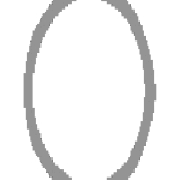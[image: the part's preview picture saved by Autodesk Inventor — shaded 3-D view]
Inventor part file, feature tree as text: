
AUTODESK INVENTOR PART (.ipt)
format: ipt  version: 2021 (Build 250183000, 183)  size: 112,128 bytes
history: native  units: in
note: dims shown in document units (in); Inventor stores cm internally (conversion verified against a paired STEP export)
features: other x4, sketch x3, plane x1
ambient origin geometry x8: Origin, YZ Plane, XZ Plane, XY Plane, X Axis, Y Axis, Z Axis, Center Point
bodies: Solid1 (feature_tree), Body (feature_tree)
feature tree (8):
  other  "Driven Length"
  other  "Frame Generator"
  other  "Start Plane"
  other  "End Plane"
  sketch  "Sketch"  dims[d2=21.5in d4=-0.0in d5=21.5in d6=0.12in d7=0.0in d8=90.0deg d9=21.5in]
  sketch  "Sketch2"  dims[d0=1.0in]
  plane  "Work Plane3"
  sketch  "Sketch3"  dims[d1=0.065in]
